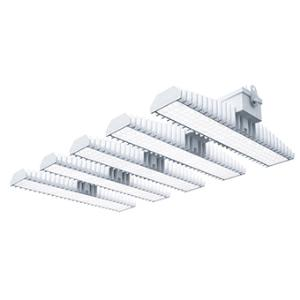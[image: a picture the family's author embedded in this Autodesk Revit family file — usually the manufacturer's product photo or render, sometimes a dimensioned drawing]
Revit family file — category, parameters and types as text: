
# Revit family: 3f_filippi_-_3f_lem_ampio_3f_filippi_-_58886_a0812_-_3f_lem_5_led_250_cr_ampio___vs_bf61
name_source: partatom
category: Lighting Fixtures
units: mm (PartAtom-declared; Revit-internal decimal feet)

## family parameters
Cut with Voids When Loaded = No
Host = Face
Light Source = No
Part Type = Normal
Room Calculation Point = No
Round Connector Dimension = Use Diameter
Shared = No

## types (1)
- 3F Filippi - 3F LEM Ampio (1 x LED, 33259 lm, 274 W, 4000 K)
    Apparent Load = 274 VA
    Approval mark = CE
    CIE Flux Codes = 67 90 97 100 100
    Color Rendering = 80
    Color Temperature = 4000 K
    Control Gear = Electronic ballast
    Default Elevation = 1800 mm
    Description = Industrial luminaire with high light output and high luminous efficiency designed with the most innovative technologies for environments with temperature up to 55°C.

ILLUMINOTECHNICAL
Luminous efficiency 100% (DLOR 98%, ULOR 2%).
Initial luminous flux of the luminaire 33259 lm.
Direct symmetric wide distribution: the illuminated area has a rectangular shape.
Installation Interdistance Transv.D = 1.24 x hu - Long.D = 1.20 x hu.
Tabular UGR (CIE 117 - 4H-8H; S=0.25H; 70/50/20): RUG 22.8 - 22.9.
Beam angle: 82° - 83°.
Luminous efficacy 121 lm/W.
Lifetime (L93/B10): 30000 h. (tq+25°C)
Lifetime (L90/B10): 50000 h. (tq+25°C)
Lifetime (L85/B10): 80000 h. (tq+25°C)
Lifetime (L80/B10): 100000 h. (tq+25°C)
Lifetime (L85/B10): 50000 h. (tq+55°C)
Sudden decreased luminous flux after 50000 hours: 0% (C0).
Photobiological safety in compliance with IEC/TR 62778: RG0 risk exempt, (IEC 62471).
In compliance with IEC/EN 62722-2-1 - IEC/EN 62717 standards.

SOURCE
5 Mid-Power linear LED modules 50W/840.
Energy efficiency class (UE 2019/2020 - UE 2019/2015): C.
CIE 13.3 Colour rendering index: CRI >80 (R9 <50%).
IES TM-30 Fidelity Index: Rf = 84 Rg = 95.
CCT nominal colour temperature 4000 K.
Colour initial tolerance (MacAdam): SDCM 3.

MECHANICAL
Passive modular heatsinks in die-casted aluminium, painted in white colour.
To optimize the thermal management of the LED module, the heatsinks are oversized and provided with self-cleaning of cooling fins.
Wiring body in aluminium and galvanised steel anchored solidly to the sinks and thermally separated.
3F Lens lenses with high luminous efficiency, transparent methacrylate (PMMA), fixed to the LED modules.
Fixing brackets in stainless steel.
Luminaire with limited surface temperature. - D - (EN 60598-2-24)
Dimensions: 952x542 mm, height 133 mm. Weight 23.325 kg.
IP65 protection degree.
Mechanical strength to impacts IK06 (1 joule).
Glow-wire test resistance 650°C.

ELECTRICAL
Halogen Free electronic wiring 230V-50/60Hz, power factor 0.97, THD <25%, constant output current, class I, 3 driver.
Power of the luminaire 274 W.
ENEC - CE.
SAFE FLICKER: PstLM=<1 and SVM=<0.4 (IEC TR 61547-1 and IEC TR 63158), to ensure a more comfortable and safe light.
Luminaire compliant with EN 60598-2-22 for power supply from a centralised emergency system CPSS (Central Power Supply System), not incorporated in the luminaire - high risk areas excluded. The default power and flux are 100% in AC and 100% in DC.
Ambient temperature from -30°C to +55°C.
Temperature class T6 max 85°C.
Quick connection via M20 3P connector with 9-13 mm tightening range.
Power unit positioned on a separate compartment by the LED module to ensure optimum temperatures of cabling components, to be inspectable and maintainable.
Relative humidity UR: <85%.

INSTALLATION
Ceiling / Suspended / Wall.
All accessories dedicated to this product are available on the Catalog and on our website www.3F-Filippi.com.

ACCESSORIES
A0812 - Anti-glare microprismatic VS moulded glass, tempered, not flammable, with sealing gasket.
One required for each light module. The pack contains 10 pieces.

APPLICATIONS
In commercial environments, exhibition and industrial areas, stores, open areas.
Applications with high ambient temperature up to 55°C.
Environments in which it is necessary a total protection against falling fragments (eg environments with foodstuffs or machines with moving parts or with extreme temperature changes), use luminaires with polycarbonate lenses.

WARNING
Fixture not suitable for cold stores with an ambient temperature <0°C and/or relative humidity >85%.
Luminaire designed for disposal/recycling at end-of-life.
Replaceable (LED only) light source by a professional. Replaceable control gear by a professional.
    Height = 133 mm  [stored 0.436352 ft]
    Lamp = 1 x LED
    Lamp Light Flux = 33259 lm
    Lamp Power = 274 W
    Lamp count = 1
    Length = 952 mm
    Lifetime = 50000 h
    Luminous efficacy = 121 lm/W
    Manufacturer = 3F Filippi
    ModVariant = No
    Model = 3F Filippi - 58886+A0812 - 3F LEM 5 LED 250 CR AMPIO + VS
    Mounting Place = Ceiling
    Mounting Type = Pendant
    Number of Poles = 1
    OnlyDefault = Yes
    Power Factor = 1
    Product Name = 3F Filippi - 3F LEM Ampio
    Product group = pendant luminaire
    ProductGroupID = 9
    Protection Class = Protection class I
    Protection Degree = IP 65
    RLX_Detail_Level = 1
    RLX_Emergency_Light_Flux = 0 lm
    RLX_Emergency_Type = 0
    RLX_Emergency_Type_DB = No
    RlxData = <blob elided: 130185 chars, md5=0707f137>
    Socket = socket
    Standby Power = 0 W
    System Light Flux = 33259 lm
    System Power = 274 W
    Type Comments = Product without accessories
    Type Image = 3f_filippi_-_lem_5__a0812.jpg
    URL = http://relux.com
    VarID = ---
    Voltage = 0 V
    Weight = 0.00 kg
    Width = 542 mm

note: [stored X ft] marks values corroborated as IEEE doubles in the binary element streams (Revit-internal decimal feet)

## geometry (parser evidence)
native form markers: Blend x4, Sweep x11
no freeform markers — native parametric forms only
